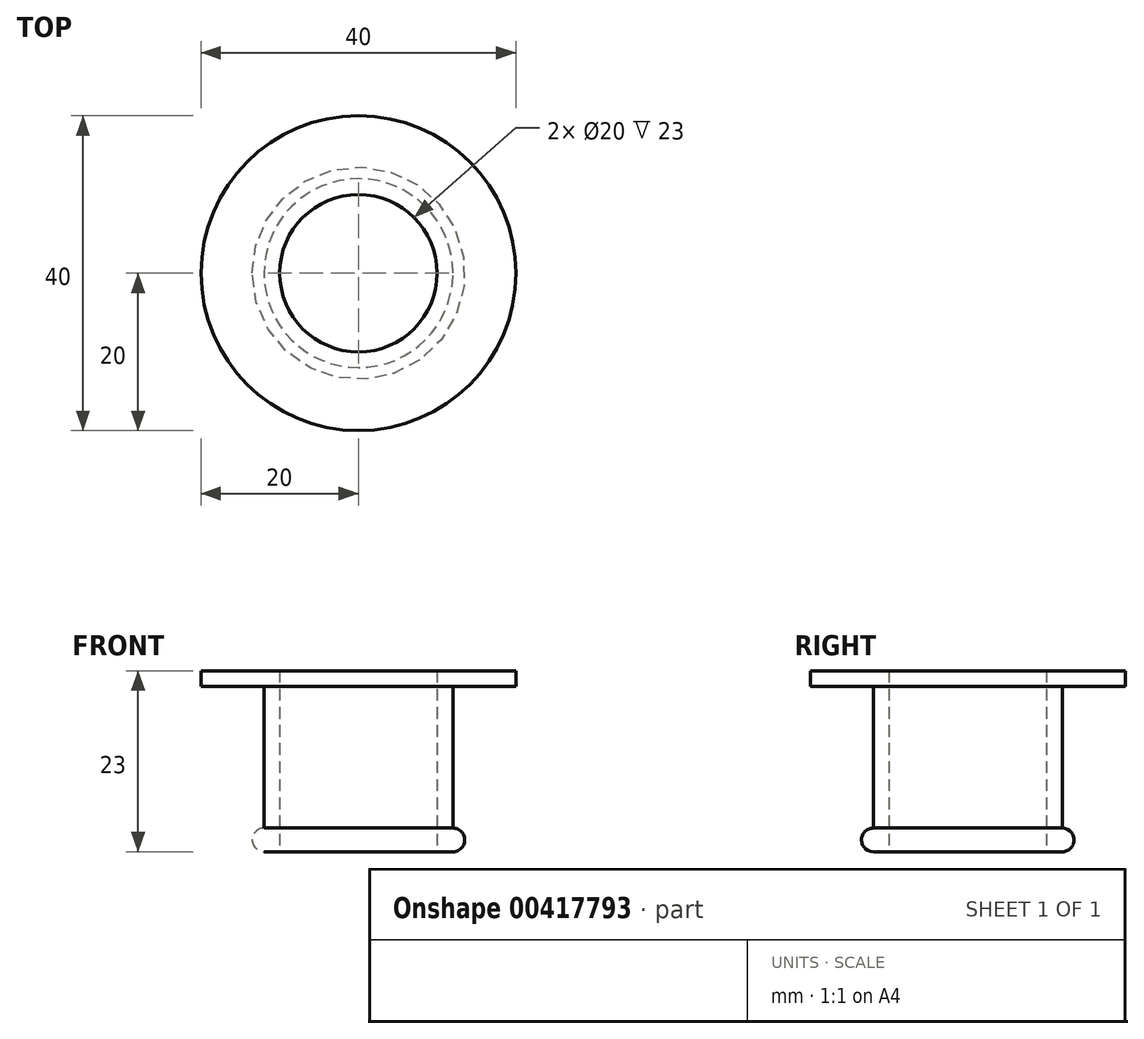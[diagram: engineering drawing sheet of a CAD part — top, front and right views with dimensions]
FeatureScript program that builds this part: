
annotation { "Feature Type Name" : "Feature", "Feature Type Description" : "" }
export const myFeature = defineFeature(function(context is Context, id is Id, definition is map)
    precondition{}
    {
        {
            var Q0;
            Q0=qCreatedBy(makeId("Front.planeOp"),FACE);
            var sketch = newSketch(context, id + "F0", { "sketchPlane" : qUnion([Q0])});
            skLineSegment(sketch, "E0", {"start": v(-10, -0.05) * mm, "end": v(-10, 22.95) * mm});
            skLineSegment(sketch, "E1", {"start": v(-10, 22.95) * mm, "end": v(-20, 22.95) * mm});
            skLineSegment(sketch, "E2", {"start": v(-20, 22.95) * mm, "end": v(-20, 20.95) * mm});
            skLineSegment(sketch, "E3", {"start": v(-20, 20.95) * mm, "end": v(-12, 20.95) * mm});
            skLineSegment(sketch, "E4", {"start": v(-12, 20.95) * mm, "end": v(-12, 2.95) * mm});
            skArc(sketch, "E5", {"start": v(-12, 2.95) * mm, "mid": v(-13.5, 1.45) * mm, "end": v(-12, -0.05) * mm});
            skLineSegment(sketch, "E6", {"start": v(-12, -0.05) * mm, "end": v(-10, -0.05) * mm});
            skLineSegment(sketch, "E7", {"start": v(0, 0) * mm, "end": v(0, 9.8) * mm});
            skSolve(sketch);
        }
        {
            var Q0;
            Q0 = qSketchRegion(id + "F0", true);
            var Q1;
            Q1=sQuery(id+"F0.wireOp",EDGE,"E7");
            revolve(context, id + "F1", {"entities" : qUnion([Q0]), "axis" : qUnion([Q1]), "revolveType" : RevolveType.FULL});
        }
    });
